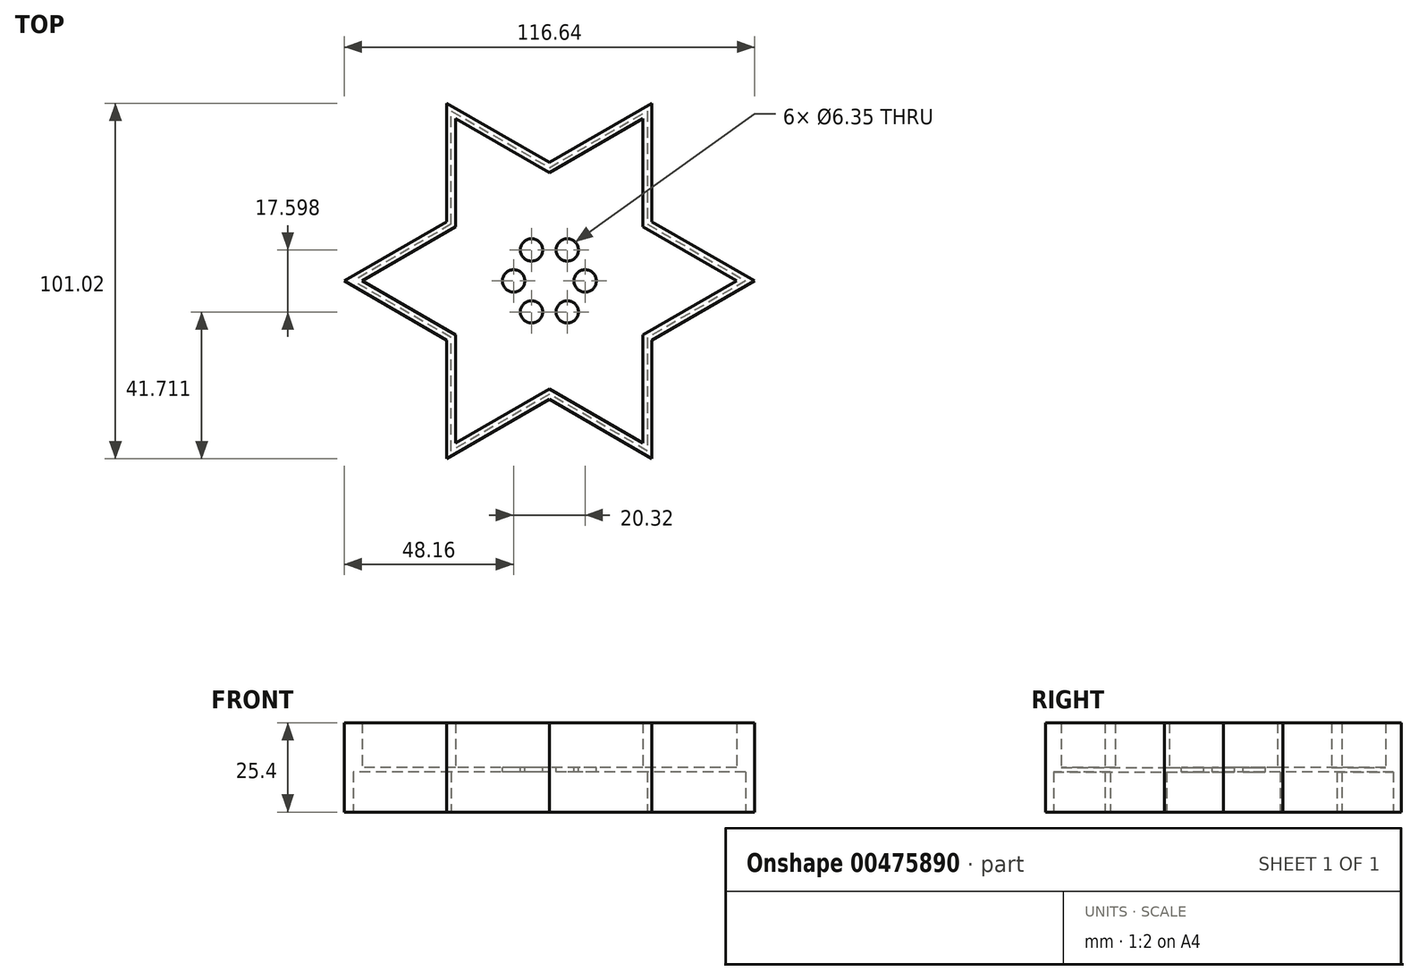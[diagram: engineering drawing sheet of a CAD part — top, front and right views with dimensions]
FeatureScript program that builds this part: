
annotation { "Feature Type Name" : "Feature", "Feature Type Description" : "" }
export const myFeature = defineFeature(function(context is Context, id is Id, definition is map)
    precondition{}
    {
        {
            var Q0;
            Q0=qCreatedBy(makeId("Top.planeOp"),FACE);
            var sketch = newSketch(context, id + "F0", { "sketchPlane" : qUnion([Q0])});
            skCircle(sketch, "E0.cCircle", {"center": v(0, 0) * mm, "radius": 29.16 * mm, "construction": true});
            skLineSegment(sketch, "E0.0", {"start": v(29.16, 50.5) * mm, "end": v(29.16, -50.5) * mm, "construction": true});
            skLineSegment(sketch, "E0.1", {"start": v(29.16, -50.5) * mm, "end": v(-58.32, 0) * mm, "construction": true});
            skLineSegment(sketch, "E0.2", {"start": v(-58.32, 0) * mm, "end": v(29.16, 50.5) * mm, "construction": true});
            skPoint(sketch, "E0.0.midPoint", {"position": v(29.16, 0) * mm});
            skLineSegment(sketch, "E1.0", {"start": v(-29.16, -50.5) * mm, "end": v(-29.16, 50.5) * mm, "construction": true});
            skLineSegment(sketch, "E1.1", {"start": v(-29.16, 50.5) * mm, "end": v(58.32, 0) * mm, "construction": true});
            skLineSegment(sketch, "E1.2", {"start": v(58.32, 0) * mm, "end": v(-29.16, -50.5) * mm, "construction": true});
            skPoint(sketch, "E1.0.midPoint", {"position": v(-29.16, 0) * mm});
            skPoint(sketch, "E2", {"position": v(-29.16, -16.84) * mm});
            skPoint(sketch, "E3", {"position": v(0, -33.67) * mm});
            skPoint(sketch, "E4", {"position": v(29.16, -16.84) * mm});
            skPoint(sketch, "E5", {"position": v(29.16, 16.84) * mm});
            skPoint(sketch, "E6", {"position": v(0, 33.67) * mm});
            skPoint(sketch, "E7", {"position": v(-29.16, 16.84) * mm});
            skLineSegment(sketch, "E8", {"start": v(-29.16, -16.84) * mm, "end": v(-58.32, 0) * mm});
            skLineSegment(sketch, "E9", {"start": v(-29.16, 16.84) * mm, "end": v(-58.32, 0) * mm});
            skLineSegment(sketch, "E10", {"start": v(-29.16, 16.84) * mm, "end": v(-29.16, 50.5) * mm});
            skLineSegment(sketch, "E11", {"start": v(-29.16, 50.5) * mm, "end": v(0, 33.67) * mm});
            skLineSegment(sketch, "E12", {"start": v(0, 33.67) * mm, "end": v(29.16, 50.5) * mm});
            skLineSegment(sketch, "E13", {"start": v(29.16, 50.5) * mm, "end": v(29.16, 16.84) * mm});
            skLineSegment(sketch, "E14", {"start": v(29.16, 16.84) * mm, "end": v(58.32, 0) * mm});
            skLineSegment(sketch, "E15", {"start": v(58.32, 0) * mm, "end": v(29.16, -16.84) * mm});
            skLineSegment(sketch, "E16", {"start": v(29.16, -16.84) * mm, "end": v(29.16, -50.5) * mm});
            skLineSegment(sketch, "E17", {"start": v(29.16, -50.5) * mm, "end": v(0, -33.67) * mm});
            skLineSegment(sketch, "E18", {"start": v(0, -33.67) * mm, "end": v(-29.16, -50.5) * mm});
            skLineSegment(sketch, "E19", {"start": v(-29.16, -50.5) * mm, "end": v(-29.16, -16.84) * mm});
            skSolve(sketch);
        }
        {
            var Q0;
            Q0=makeQuery(id+"F0.imprint","IMPRINT",FACE,{"disambiguationData":[TD([[makeQuery(id+"F0.imprint","IMPRINT",EDGE,{"derivedFrom":sQuery(id+"F0.wireOp",EDGE,"E8")}),-1.0]])]});
            extrude(context, id + "F1", {"entities" : qUnion([Q0]), "depth" : 25.4 * mm});
        }
        {
            var Q0;
            Q0=makeQuery(id+"F1.opExtrude","CAP_FACE",FACE,{"disambiguationData":[OSD([sQuery(id+"F0.wireOp",EDGE,"E8"),sQuery(id+"F0.wireOp",EDGE,"E9"),sQuery(id+"F0.wireOp",EDGE,"E10"),sQuery(id+"F0.wireOp",EDGE,"E11"),sQuery(id+"F0.wireOp",EDGE,"E12"),sQuery(id+"F0.wireOp",EDGE,"E13"),sQuery(id+"F0.wireOp",EDGE,"E14"),sQuery(id+"F0.wireOp",EDGE,"E15"),sQuery(id+"F0.wireOp",EDGE,"E16"),sQuery(id+"F0.wireOp",EDGE,"E17"),sQuery(id+"F0.wireOp",EDGE,"E18"),sQuery(id+"F0.wireOp",EDGE,"E19")])],"isStart":false});
            shell(context, id + "F2", {"entities" : qUnion([Q0]), "thickness" : 2.54 * mm});
        }
        {
            var Q0;
            Q0 = qSketchRegion(id + "F0", true);
            extrude(context, id + "F3", {"entities" : qUnion([Q0]), "operationType" : NewBodyOperationType.ADD, "depth" : 12.7 * mm});
        }
        {
            var Q0;
            Q0=makeQuery(id+"F1.opExtrude","CAP_FACE",FACE,{"disambiguationData":[OSD([sQuery(id+"F0.wireOp",EDGE,"E8"),sQuery(id+"F0.wireOp",EDGE,"E9"),sQuery(id+"F0.wireOp",EDGE,"E10"),sQuery(id+"F0.wireOp",EDGE,"E11"),sQuery(id+"F0.wireOp",EDGE,"E12"),sQuery(id+"F0.wireOp",EDGE,"E13"),sQuery(id+"F0.wireOp",EDGE,"E14"),sQuery(id+"F0.wireOp",EDGE,"E15"),sQuery(id+"F0.wireOp",EDGE,"E16"),sQuery(id+"F0.wireOp",EDGE,"E17"),sQuery(id+"F0.wireOp",EDGE,"E18"),sQuery(id+"F0.wireOp",EDGE,"E19")])],"isStart":true});
            shell(context, id + "F4", {"entities" : qUnion([Q0]), "thickness" : 1.27 * mm});
        }
        {
            var Q0;
            Q0=makeQuery(id+"F3.opExtrude","CAP_FACE",FACE,{"disambiguationData":[OSD([sQuery(id+"F0.wireOp",EDGE,"E8"),sQuery(id+"F0.wireOp",EDGE,"E9"),sQuery(id+"F0.wireOp",EDGE,"E10"),sQuery(id+"F0.wireOp",EDGE,"E11"),sQuery(id+"F0.wireOp",EDGE,"E12"),sQuery(id+"F0.wireOp",EDGE,"E13"),sQuery(id+"F0.wireOp",EDGE,"E14"),sQuery(id+"F0.wireOp",EDGE,"E15"),sQuery(id+"F0.wireOp",EDGE,"E16"),sQuery(id+"F0.wireOp",EDGE,"E17"),sQuery(id+"F0.wireOp",EDGE,"E18"),sQuery(id+"F0.wireOp",EDGE,"E19")])],"isStart":false});
            var sketch = newSketch(context, id + "F5", { "sketchPlane" : qUnion([Q0])});
            skLineSegment(sketch, "E20", {"start": v(26.62, 46.1) * mm, "end": v(0, 0) * mm, "construction": true});
            skLineSegment(sketch, "E21", {"start": v(0, 0) * mm, "end": v(53.24, 0) * mm, "construction": true});
            skLineSegment(sketch, "E22", {"start": v(53.24, 0) * mm, "end": v(-53.24, 0) * mm, "construction": true});
            skLineSegment(sketch, "E23", {"start": v(-53.24, 0) * mm, "end": v(0, 0) * mm, "construction": true});
            skLineSegment(sketch, "E24", {"start": v(-26.62, 46.1) * mm, "end": v(26.62, -46.1) * mm, "construction": true});
            skLineSegment(sketch, "E25", {"start": v(26.62, -46.1) * mm, "end": v(0, 0) * mm, "construction": true});
            skLineSegment(sketch, "E26", {"start": v(-26.62, -46.1) * mm, "end": v(0, 0) * mm, "construction": true});
            skLineSegment(sketch, "E27", {"start": v(0, 0) * mm, "end": v(5.08, 8.8) * mm, "construction": true});
            skLineSegment(sketch, "E28", {"start": v(0, 0) * mm, "end": v(10.16, 0) * mm, "construction": true});
            skLineSegment(sketch, "E29", {"start": v(0, 0) * mm, "end": v(5.08, -8.8) * mm, "construction": true});
            skLineSegment(sketch, "E30", {"start": v(0, 0) * mm, "end": v(-10.16, 0) * mm, "construction": true});
            skLineSegment(sketch, "E31", {"start": v(0, 0) * mm, "end": v(-5.08, 8.8) * mm, "construction": true});
            skCircle(sketch, "E32", {"center": v(5.08, 8.8) * mm, "radius": 3.18 * mm});
            skCircle(sketch, "E33", {"center": v(10.16, 0) * mm, "radius": 3.18 * mm});
            skCircle(sketch, "E34", {"center": v(5.08, -8.8) * mm, "radius": 3.18 * mm});
            skLineSegment(sketch, "E35", {"start": v(0, 0) * mm, "end": v(-5.08, -8.8) * mm, "construction": true});
            skCircle(sketch, "E36", {"center": v(-5.08, -8.8) * mm, "radius": 3.18 * mm});
            skCircle(sketch, "E37", {"center": v(-10.16, 0) * mm, "radius": 3.18 * mm});
            skCircle(sketch, "E38", {"center": v(-5.08, 8.8) * mm, "radius": 3.18 * mm});
            skSolve(sketch);
        }
        {
            var Q0;
            Q0=makeQuery(id+"F5.imprint","IMPRINT",FACE,{"disambiguationData":[TD([[makeQuery(id+"F5.imprint","IMPRINT",EDGE,{"derivedFrom":sQuery(id+"F5.wireOp",EDGE,"E32")}),1.0]])]});
            var Q1;
            Q1=makeQuery(id+"F5.imprint","IMPRINT",FACE,{"disambiguationData":[TD([[makeQuery(id+"F5.imprint","IMPRINT",EDGE,{"derivedFrom":sQuery(id+"F5.wireOp",EDGE,"E33")}),1.0]])]});
            var Q2;
            Q2=makeQuery(id+"F5.imprint","IMPRINT",FACE,{"disambiguationData":[TD([[makeQuery(id+"F5.imprint","IMPRINT",EDGE,{"derivedFrom":sQuery(id+"F5.wireOp",EDGE,"E34")}),1.0]])]});
            var Q3;
            Q3=makeQuery(id+"F5.imprint","IMPRINT",FACE,{"disambiguationData":[TD([[makeQuery(id+"F5.imprint","IMPRINT",EDGE,{"derivedFrom":sQuery(id+"F5.wireOp",EDGE,"E36")}),1.0]])]});
            var Q4;
            Q4=makeQuery(id+"F5.imprint","IMPRINT",FACE,{"disambiguationData":[TD([[makeQuery(id+"F5.imprint","IMPRINT",EDGE,{"derivedFrom":sQuery(id+"F5.wireOp",EDGE,"E37")}),1.0]])]});
            var Q5;
            Q5=makeQuery(id+"F5.imprint","IMPRINT",FACE,{"disambiguationData":[TD([[makeQuery(id+"F5.imprint","IMPRINT",EDGE,{"derivedFrom":sQuery(id+"F5.wireOp",EDGE,"E38")}),1.0]])]});
            extrude(context, id + "F6", {"entities" : qUnion([Q0, Q1, Q2, Q3, Q4, Q5]), "operationType" : NewBodyOperationType.REMOVE, "oppositeDirection" : true, "depth" : 25.4 * mm});
        }
    });
